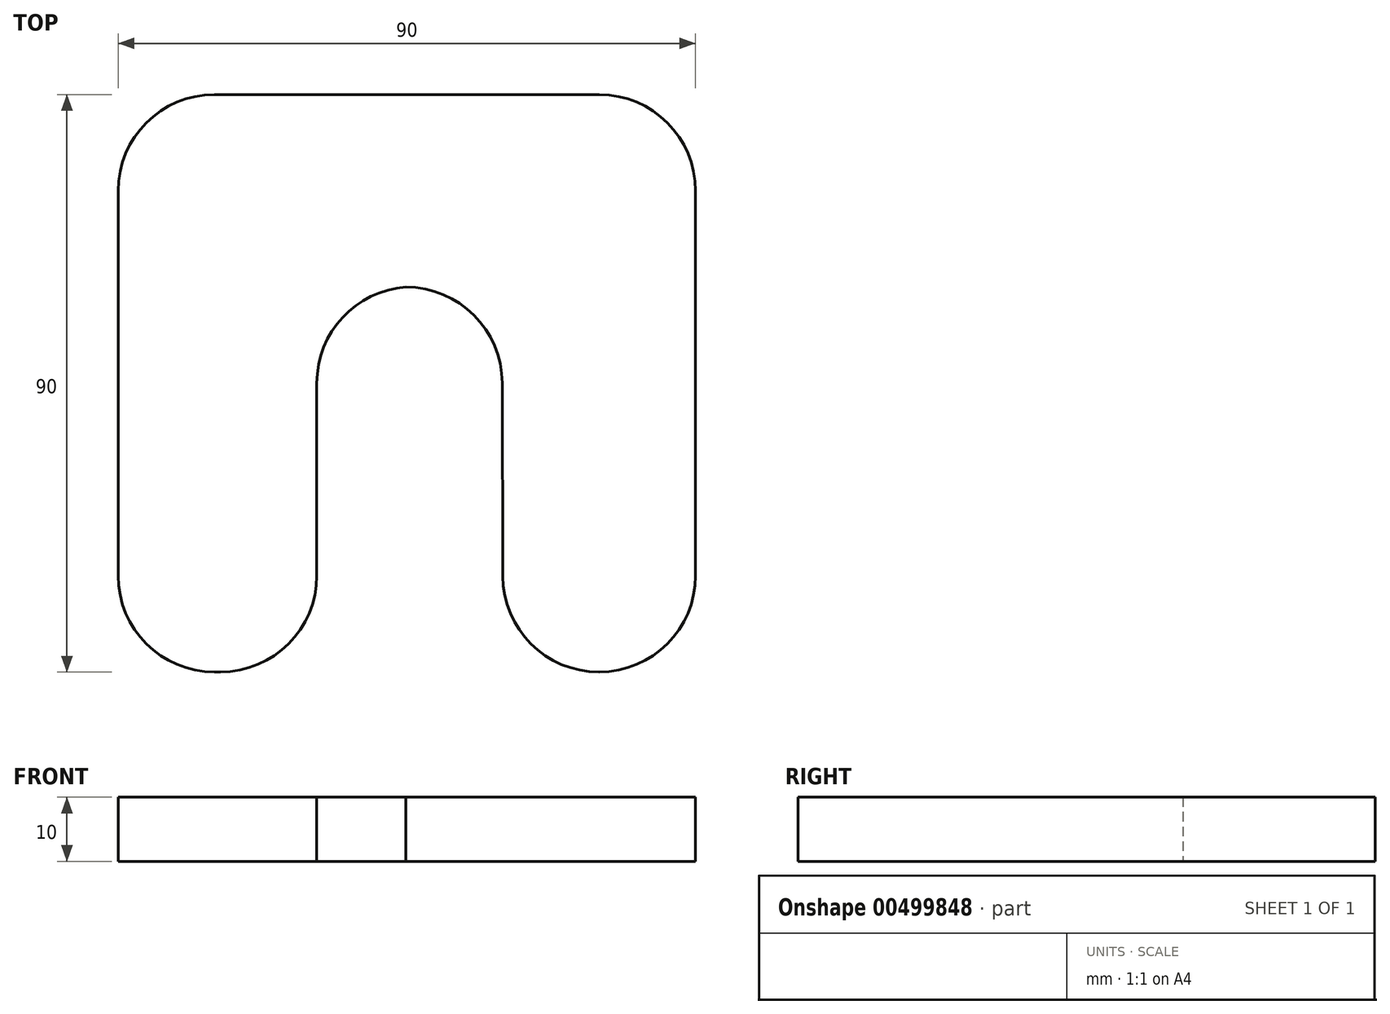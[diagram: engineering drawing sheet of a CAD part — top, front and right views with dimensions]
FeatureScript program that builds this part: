
annotation { "Feature Type Name" : "Feature", "Feature Type Description" : "" }
export const myFeature = defineFeature(function(context is Context, id is Id, definition is map)
    precondition{}
    {
        {
            var Q0;
            Q0=qCreatedBy(makeId("Top.planeOp"),FACE);
            var sketch = newSketch(context, id + "F0", { "sketchPlane" : qUnion([Q0])});
            skLineSegment(sketch, "E0.bottom", {"start": v(0, 0) * mm, "end": v(30.96, 0) * mm});
            skLineSegment(sketch, "E0.top", {"start": v(0, 90) * mm, "end": v(90, 90) * mm});
            skLineSegment(sketch, "E0.left", {"start": v(0, 0) * mm, "end": v(0, 90) * mm});
            skLineSegment(sketch, "E0.right", {"start": v(90, 0) * mm, "end": v(90, 90) * mm});
            skLineSegment(sketch, "E1.trimOffspring", {"start": v(60, 0) * mm, "end": v(90, 0) * mm});
            skLineSegment(sketch, "E2", {"start": v(30.96, 0) * mm, "end": v(30.96, 60) * mm});
            skLineSegment(sketch, "E3", {"start": v(30.96, 60) * mm, "end": v(59.81, 60) * mm});
            skLineSegment(sketch, "E4", {"start": v(60, 0) * mm, "end": v(59.81, 60) * mm});
            skSolve(sketch);
        }
        {
            var Q0;
            Q0 = qSketchRegion(id + "F0", true);
            var Q1;
            Q1=makeQuery(id+"F0.imprint","IMPRINT",FACE,{"disambiguationData":[TD([[makeQuery(id+"F0.imprint","IMPRINT",EDGE,{"derivedFrom":sQuery(id+"F0.wireOp",EDGE,"E0.bottom")}),1.0]])]});
            extrude(context, id + "F1", {"entities" : qUnion([Q0, Q1]), "depth" : 10 * mm});
        }
        {
            var Q0;
            Q0=makeQuery(id+"F1.opExtrude","SWEPT_EDGE",EDGE,{"disambiguationData":[OSD([sQuery(id+"F0.wireOp",EDGE,"E0.top"),sQuery(id+"F0.wireOp",EDGE,"E0.left")])]});
            var Q1;
            Q1=makeQuery(id+"F1.opExtrude","SWEPT_EDGE",EDGE,{"disambiguationData":[OSD([sQuery(id+"F0.wireOp",EDGE,"E0.top"),sQuery(id+"F0.wireOp",EDGE,"E0.right")])]});
            fillet(context, id + "F2", {"entities" : qUnion([Q0, Q1]), "radius" : 15 * mm, "tangentPropagation" : true, "allowEdgeOverflow" : false});
        }
        {
            var Q0;
            Q0=makeQuery(id+"F1.opExtrude","SWEPT_EDGE",EDGE,{"disambiguationData":[OSD([sQuery(id+"F0.wireOp",EDGE,"E0.bottom"),sQuery(id+"F0.wireOp",EDGE,"E0.left")])]});
            var Q1;
            Q1=makeQuery(id+"F1.opExtrude","SWEPT_EDGE",EDGE,{"disambiguationData":[OSD([sQuery(id+"F0.wireOp",EDGE,"E0.bottom"),sQuery(id+"F0.wireOp",EDGE,"E2")])]});
            fillet(context, id + "F3", {"entities" : qUnion([Q0, Q1]), "radius" : 15 * mm, "tangentPropagation" : true, "allowEdgeOverflow" : false});
        }
        {
            var Q0;
            Q0=makeQuery(id+"F1.opExtrude","SWEPT_EDGE",EDGE,{"disambiguationData":[OSD([sQuery(id+"F0.wireOp",EDGE,"E1.trimOffspring"),sQuery(id+"F0.wireOp",EDGE,"E4")])]});
            var Q1;
            Q1=makeQuery(id+"F1.opExtrude","SWEPT_EDGE",EDGE,{"disambiguationData":[OSD([sQuery(id+"F0.wireOp",EDGE,"E0.right"),sQuery(id+"F0.wireOp",EDGE,"E1.trimOffspring")])]});
            fillet(context, id + "F4", {"entities" : qUnion([Q0, Q1]), "radius" : 15 * mm, "tangentPropagation" : true, "allowEdgeOverflow" : false});
        }
        {
            var Q0;
            Q0=makeQuery(id+"F1.opExtrude","SWEPT_EDGE",EDGE,{"disambiguationData":[OSD([sQuery(id+"F0.wireOp",EDGE,"E3"),sQuery(id+"F0.wireOp",EDGE,"E4")])]});
            fillet(context, id + "F5", {"entities" : qUnion([Q0]), "radius" : 15 * mm, "tangentPropagation" : true, "allowEdgeOverflow" : false});
        }
        {
            var Q0;
            Q0=makeQuery(id+"F1.opExtrude","SWEPT_EDGE",EDGE,{"disambiguationData":[OSD([sQuery(id+"F0.wireOp",EDGE,"E2"),sQuery(id+"F0.wireOp",EDGE,"E3")])]});
            fillet(context, id + "F6", {"entities" : qUnion([Q0]), "radius" : 15 * mm, "tangentPropagation" : true, "allowEdgeOverflow" : false});
        }
    });
